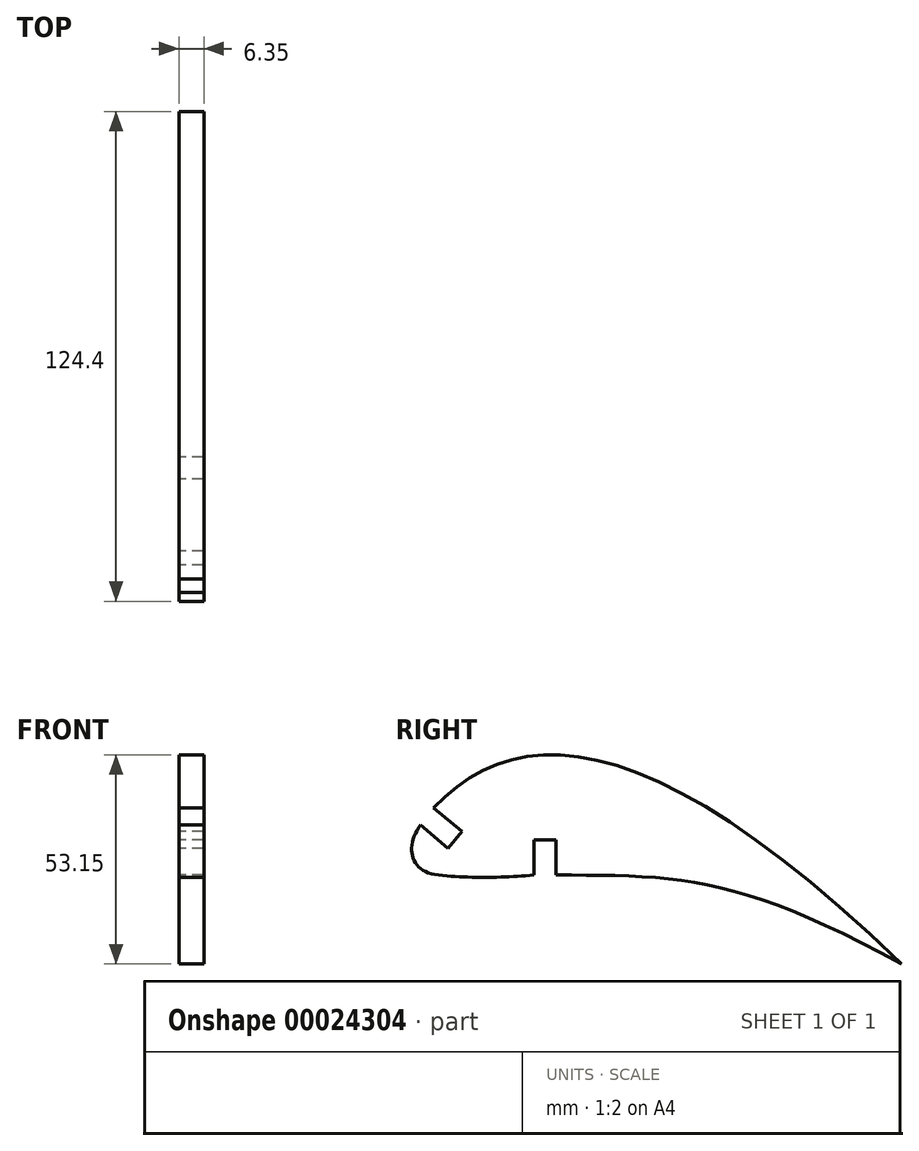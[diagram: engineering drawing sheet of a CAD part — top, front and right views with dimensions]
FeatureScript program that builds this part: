
annotation { "Feature Type Name" : "Feature", "Feature Type Description" : "" }
export const myFeature = defineFeature(function(context is Context, id is Id, definition is map)
    precondition{}
    {
        {
            var Q0;
            Q0=qCreatedBy(makeId("Right.planeOp"),FACE);
            var sketch = newSketch(context, id + "F0", { "sketchPlane" : qUnion([Q0])});
            skLineSegment(sketch, "E0", {"start": v(36.65, 0) * mm, "end": v(36.65, 8.94) * mm, "construction": true});
            skLineSegment(sketch, "E1", {"start": v(33.88, 8.94) * mm, "end": v(39.42, 8.94) * mm});
            skLineSegment(sketch, "E2", {"start": v(33.88, 8.94) * mm, "end": v(33.88, 0) * mm});
            skLineSegment(sketch, "E3", {"start": v(39.42, 8.94) * mm, "end": v(39.42, 0) * mm});
            skLineSegment(sketch, "E4", {"start": v(39.42, 8.94) * mm, "end": v(-11.84, 8.94) * mm, "construction": true});
            skLineSegment(sketch, "E5.bottom", {"start": v(13.79, 8.94) * mm, "end": v(1.09, 8.94) * mm, "construction": true});
            skLineSegment(sketch, "E5.top", {"start": v(13.79, 19.62) * mm, "end": v(1.09, 19.62) * mm, "construction": true});
            skLineSegment(sketch, "E5.left", {"start": v(13.79, 8.94) * mm, "end": v(13.79, 19.62) * mm, "construction": true});
            skLineSegment(sketch, "E5.right", {"start": v(1.09, 8.94) * mm, "end": v(1.09, 19.62) * mm, "construction": true});
            skLineSegment(sketch, "E6", {"start": v(1.09, 19.62) * mm, "end": v(13.79, 8.94) * mm, "construction": true});
            skLineSegment(sketch, "E7", {"start": v(15.57, 11.06) * mm, "end": v(12, 6.82) * mm});
            skLineSegment(sketch, "E8", {"start": v(15.57, 11.06) * mm, "end": v(8.4, 17.08) * mm});
            skLineSegment(sketch, "E9", {"start": v(12, 6.82) * mm, "end": v(5, 12.7) * mm});
            skPoint(sketch, "E10.visualSharp", {"position": v(5, 12.7) * mm});
            skPoint(sketch, "E11.trimOffspring.0.internal.orphan", {"position": v(0, 0) * mm});
            skPoint(sketch, "E12.visualSharp", {"position": v(0, -5.13) * mm});
            skPoint(sketch, "E13.startDerivative.orphan", {"position": v(0, 41.82) * mm});
            skPoint(sketch, "E14.end.orphan", {"position": v(51.52, 39.09) * mm});
            skLineSegment(sketch, "E15", {"start": v(15.57, 11.06) * mm, "end": v(-12.16, 34.38) * mm, "construction": true});
            skPoint(sketch, "E16.visualSharp", {"position": v(1.93, -55.68) * mm});
            skArc(sketch, "E17.trimOffspring", {"start": v(28.09, -12.56) * mm, "mid": v(28.11, -12.57) * mm, "end": v(28.14, -12.59) * mm});
            skFitSpline(sketch, "E18", {"points": [v(8.4, 17.08) * mm, v(127.19, -22.57) * mm], "startDerivative": vector(64.47, 68.67) * mm, "endDerivative": vector(187.62, -181.83) * mm});
            skFitSpline(sketch, "E19", {"points": [v(9.59, 0) * mm, v(5, 12.7) * mm], "startDerivative": vector(-22.16, 2.35) * mm, "endDerivative": vector(11.76, 16.09) * mm});
            skFitSpline(sketch, "E20", {"points": [v(39.42, 0) * mm, v(127.19, -22.57) * mm], "startDerivative": vector(93.64, 0) * mm, "endDerivative": vector(123.34, -67.7) * mm});
            skLineSegment(sketch, "E21", {"start": v(127.19, 41.52) * mm, "end": v(127.19, -81.95) * mm, "construction": true});
            skLineSegment(sketch, "E22", {"start": v(2.79, 90.7) * mm, "end": v(2.79, -58.9) * mm, "construction": true});
            skLineSegment(sketch, "E23", {"start": v(-29.46, 30.58) * mm, "end": v(180.34, 30.58) * mm, "construction": true});
            skLineSegment(sketch, "E24", {"start": v(262.54, -22.57) * mm, "end": v(-20.18, -22.57) * mm, "construction": true});
            skFitSpline(sketch, "E25", {"points": [v(33.88, 0) * mm, v(9.59, 0) * mm], "startDerivative": vector(-24.2, -2.04) * mm, "endDerivative": vector(-24.58, 2.6) * mm});
            skSolve(sketch);
        }
        {
            var Q0;
            Q0=qSketchRegion(id+"F0",true);
            extrude(context, id + "F1", {"entities" : qUnion([Q0]), "depth" : 6.35 * mm});
        }
    });
